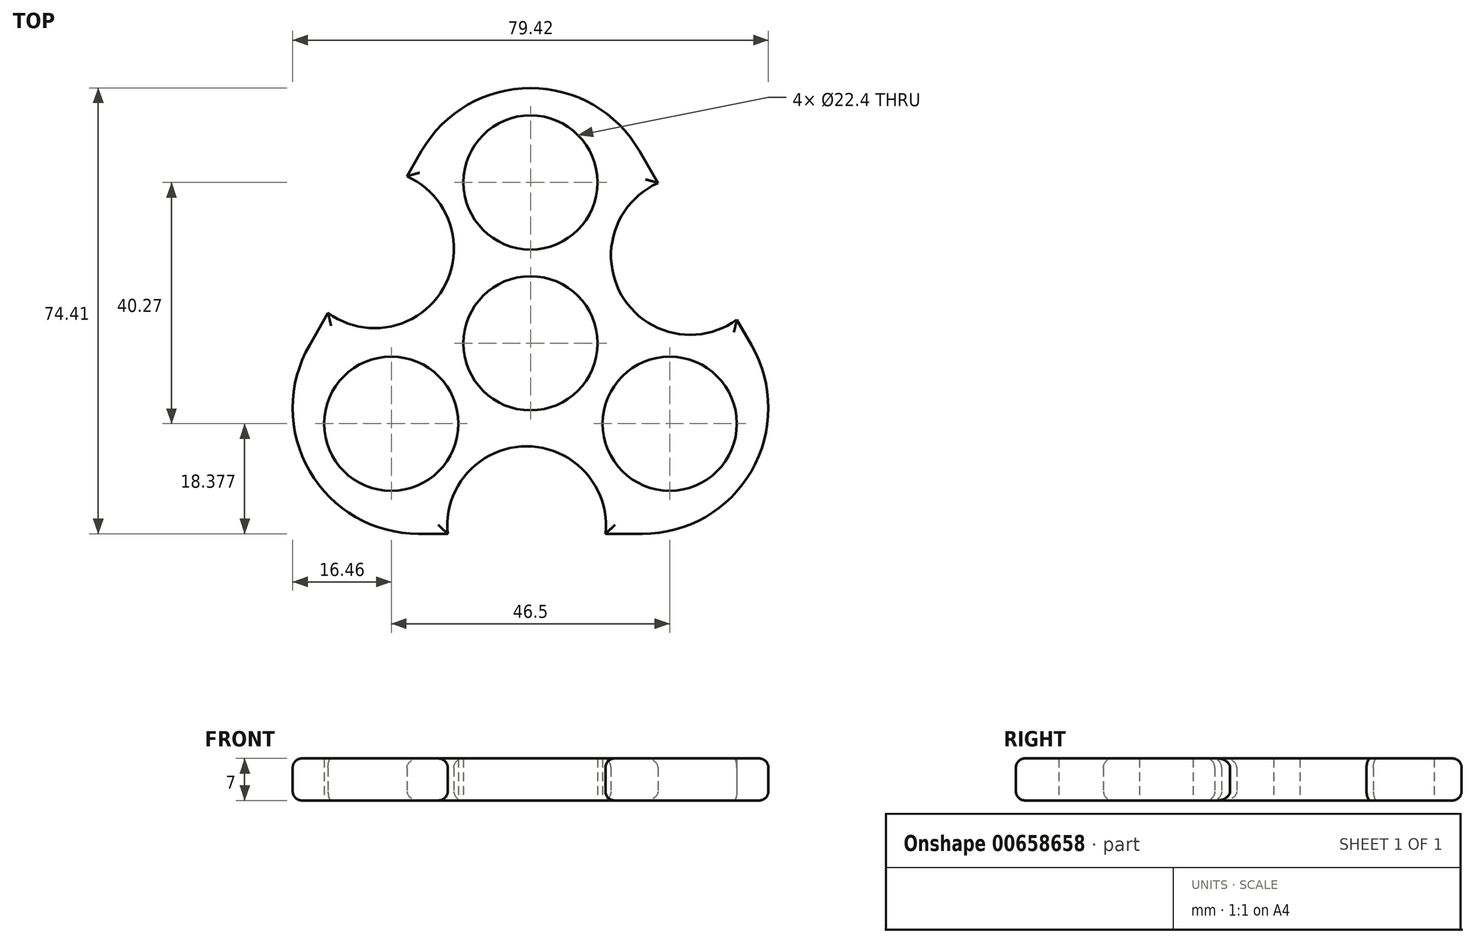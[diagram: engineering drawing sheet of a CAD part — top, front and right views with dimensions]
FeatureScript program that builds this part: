
annotation { "Feature Type Name" : "Feature", "Feature Type Description" : "" }
export const myFeature = defineFeature(function(context is Context, id is Id, definition is map)
    precondition{}
    {
        {
            var Q0;
            Q0=qCreatedBy(makeId("Top.planeOp"),FACE);
            var sketch = newSketch(context, id + "F0", { "sketchPlane" : qUnion([Q0])});
            skCircle(sketch, "E0", {"center": v(0, 0) * mm, "radius": 11.2 * mm});
            skLineSegment(sketch, "E1.0", {"start": v(55.08, -31.8) * mm, "end": v(12.52, -31.8) * mm});
            skLineSegment(sketch, "E1.1", {"start": v(-55.08, -31.8) * mm, "end": v(-33.8, 5.06) * mm});
            skLineSegment(sketch, "E1.2", {"start": v(0, 63.6) * mm, "end": v(21.28, 26.74) * mm});
            skPoint(sketch, "E1.0.midPoint", {"position": v(0, -31.8) * mm});
            skCircle(sketch, "E2", {"center": v(0, 26.85) * mm, "radius": 11.2 * mm});
            skCircle(sketch, "E3.1.0", {"center": v(-23.25, -13.42) * mm, "radius": 11.2 * mm});
            skCircle(sketch, "E3.2.0", {"center": v(23.25, -13.42) * mm, "radius": 11.2 * mm});
            skArc(sketch, "E4", {"start": v(21.28, 26.74) * mm, "mid": v(15.21, 8.03) * mm, "end": v(34.45, 3.93) * mm});
            skLineSegment(sketch, "E5.trimOffspring", {"start": v(34.45, 3.93) * mm, "end": v(55.08, -31.8) * mm});
            skArc(sketch, "E6.1.0", {"start": v(-33.8, 5.06) * mm, "mid": v(-14.56, 9.16) * mm, "end": v(-20.63, 27.87) * mm});
            skArc(sketch, "E6.2.0", {"start": v(12.52, -31.8) * mm, "mid": v(-0.65, -17.2) * mm, "end": v(-13.82, -31.8) * mm});
            skLineSegment(sketch, "E7.trimOffspring", {"start": v(-20.63, 27.87) * mm, "end": v(0, 63.6) * mm});
            skLineSegment(sketch, "E8.trimOffspring", {"start": v(-13.82, -31.8) * mm, "end": v(-55.08, -31.8) * mm});
            skSolve(sketch);
        }
        {
            var Q0;
            Q0=makeQuery(id+"F0.imprint","IMPRINT",FACE,{"disambiguationData":[TD([[makeQuery(id+"F0.imprint","IMPRINT",EDGE,{"derivedFrom":sQuery(id+"F0.wireOp",EDGE,"E0")}),-1.0]])]});
            extrude(context, id + "F1", {"entities" : qUnion([Q0]), "depth" : 7 * mm, "offsetDistance" : 25 * mm});
        }
        {
            var Q0;
            Q0=makeQuery(id+"F1.opExtrude","CAP_EDGE",EDGE,{"disambiguationData":[OSD([sQuery(id+"F0.wireOp",EDGE,"E1.1")])],"isStart":false});
            var Q1;
            Q1=makeQuery(id+"F1.opExtrude","CAP_EDGE",EDGE,{"disambiguationData":[OSD([sQuery(id+"F0.wireOp",EDGE,"E8.trimOffspring")])],"isStart":false});
            var Q2;
            Q2=makeQuery(id+"F1.opExtrude","CAP_EDGE",EDGE,{"disambiguationData":[OSD([sQuery(id+"F0.wireOp",EDGE,"E8.trimOffspring")])],"isStart":true});
            var Q3;
            Q3=makeQuery(id+"F1.opExtrude","CAP_EDGE",EDGE,{"disambiguationData":[OSD([sQuery(id+"F0.wireOp",EDGE,"E6.2.0")])],"isStart":true});
            var Q4;
            Q4=makeQuery(id+"F1.opExtrude","CAP_EDGE",EDGE,{"disambiguationData":[OSD([sQuery(id+"F0.wireOp",EDGE,"E6.2.0")])],"isStart":false});
            var Q5;
            Q5=makeQuery(id+"F1.opExtrude","CAP_EDGE",EDGE,{"disambiguationData":[OSD([sQuery(id+"F0.wireOp",EDGE,"E1.0")])],"isStart":false});
            var Q6;
            Q6=makeQuery(id+"F1.opExtrude","CAP_EDGE",EDGE,{"disambiguationData":[OSD([sQuery(id+"F0.wireOp",EDGE,"E1.0")])],"isStart":true});
            var Q7;
            Q7=makeQuery(id+"F1.opExtrude","CAP_EDGE",EDGE,{"disambiguationData":[OSD([sQuery(id+"F0.wireOp",EDGE,"E5.trimOffspring")])],"isStart":false});
            var Q8;
            Q8=makeQuery(id+"F1.opExtrude","CAP_EDGE",EDGE,{"disambiguationData":[OSD([sQuery(id+"F0.wireOp",EDGE,"E5.trimOffspring")])],"isStart":true});
            var Q9;
            Q9=makeQuery(id+"F1.opExtrude","CAP_EDGE",EDGE,{"disambiguationData":[OSD([sQuery(id+"F0.wireOp",EDGE,"E4")])],"isStart":false});
            var Q10;
            Q10=makeQuery(id+"F1.opExtrude","CAP_EDGE",EDGE,{"disambiguationData":[OSD([sQuery(id+"F0.wireOp",EDGE,"E4")])],"isStart":true});
            var Q11;
            Q11=makeQuery(id+"F1.opExtrude","CAP_EDGE",EDGE,{"disambiguationData":[OSD([sQuery(id+"F0.wireOp",EDGE,"E1.2")])],"isStart":false});
            var Q12;
            Q12=makeQuery(id+"F1.opExtrude","CAP_EDGE",EDGE,{"disambiguationData":[OSD([sQuery(id+"F0.wireOp",EDGE,"E1.2")])],"isStart":true});
            var Q13;
            Q13=makeQuery(id+"F1.opExtrude","CAP_EDGE",EDGE,{"disambiguationData":[OSD([sQuery(id+"F0.wireOp",EDGE,"E7.trimOffspring")])],"isStart":false});
            var Q14;
            Q14=makeQuery(id+"F1.opExtrude","CAP_EDGE",EDGE,{"disambiguationData":[OSD([sQuery(id+"F0.wireOp",EDGE,"E6.1.0")])],"isStart":false});
            var Q15;
            Q15=makeQuery(id+"F1.opExtrude","CAP_EDGE",EDGE,{"disambiguationData":[OSD([sQuery(id+"F0.wireOp",EDGE,"E6.1.0")])],"isStart":true});
            var Q16;
            Q16=makeQuery(id+"F1.opExtrude","CAP_EDGE",EDGE,{"disambiguationData":[OSD([sQuery(id+"F0.wireOp",EDGE,"E1.1")])],"isStart":true});
            var Q17;
            Q17=makeQuery(id+"F1.opExtrude","CAP_EDGE",EDGE,{"disambiguationData":[OSD([sQuery(id+"F0.wireOp",EDGE,"E7.trimOffspring")])],"isStart":true});
            fillet(context, id + "F2", {"entities" : qUnion([Q0, Q1, Q2, Q3, Q4, Q5, Q6, Q7, Q8, Q9, Q10, Q11, Q12, Q13, Q14, Q15, Q16, Q17]), "radius" : 1.5 * mm, "tangentPropagation" : true, "allowEdgeOverflow" : false});
        }
        {
            var Q0;
            Q0=makeQuery(id+"F1.opExtrude","SWEPT_EDGE",EDGE,{"disambiguationData":[OSD([sQuery(id+"F0.wireOp",EDGE,"E1.1"),sQuery(id+"F0.wireOp",EDGE,"E8.trimOffspring")])]});
            var Q1;
            Q1=makeQuery(id+"F1.opExtrude","SWEPT_EDGE",EDGE,{"disambiguationData":[OSD([sQuery(id+"F0.wireOp",EDGE,"E1.2"),sQuery(id+"F0.wireOp",EDGE,"E7.trimOffspring")])]});
            var Q2;
            Q2=makeQuery(id+"F1.opExtrude","SWEPT_EDGE",EDGE,{"disambiguationData":[OSD([sQuery(id+"F0.wireOp",EDGE,"E1.0"),sQuery(id+"F0.wireOp",EDGE,"E5.trimOffspring")])]});
            fillet(context, id + "F3", {"entities" : qUnion([Q0, Q1, Q2]), "radius" : 21 * mm, "tangentPropagation" : true, "allowEdgeOverflow" : false});
        }
    });
